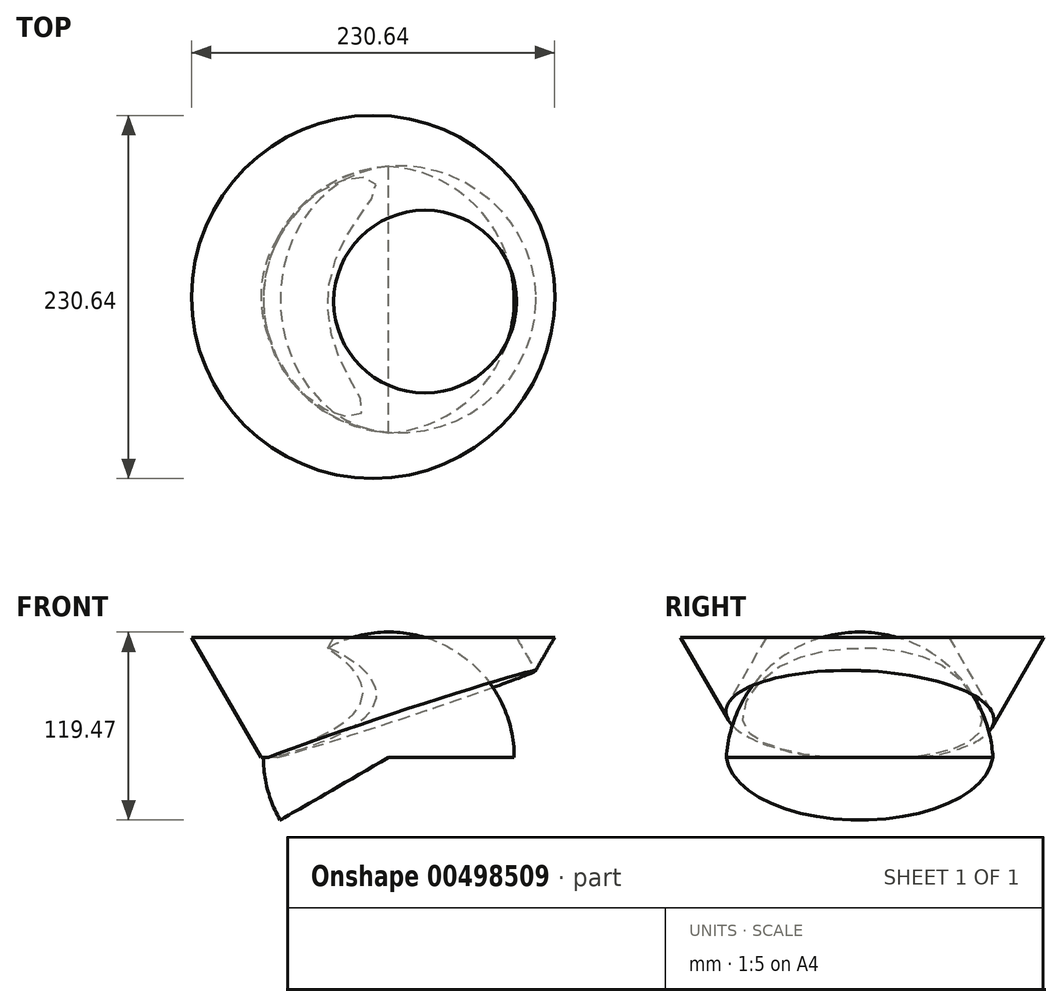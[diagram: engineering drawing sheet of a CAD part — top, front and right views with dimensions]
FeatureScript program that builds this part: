
annotation { "Feature Type Name" : "Feature", "Feature Type Description" : "" }
export const myFeature = defineFeature(function(context is Context, id is Id, definition is map)
    precondition{}
    {
        {
            var Q0;
            Q0=qCreatedBy(makeId("Top.planeOp"),FACE);
            var sketch = newSketch(context, id + "F0", { "sketchPlane" : qUnion([Q0])});
            skArc(sketch, "E0", {"start": v(5.72, 63.65) * mm, "mid": v(-4.67, 32.5) * mm, "end": v(0, 0) * mm});
            skArc(sketch, "E1", {"start": v(5.72, 63.65) * mm, "mid": v(-2.25, 32.28) * mm, "end": v(0, 0) * mm});
            skSolve(sketch);
        }
        {
            var Q0;
            Q0=makeQuery(id+"F0.imprint","IMPRINT",FACE,{"disambiguationData":[TD([[makeQuery(id+"F0.imprint","IMPRINT",EDGE,{"derivedFrom":sQuery(id+"F0.wireOp",EDGE,"E0")}),1.0]])]});
            extrude(context, id + "F1", {"entities" : qUnion([Q0]), "depth" : 76.2 * mm, "offsetDistance" : 25.4 * mm, "hasDraft" : true, "draftAngle" : 30 * degree});
        }
        {
            var Q0;
            Q0=qCreatedBy(makeId("Top.planeOp"),FACE);
            var sketch = newSketch(context, id + "F2", { "sketchPlane" : qUnion([Q0])});
            skLineSegment(sketch, "E2", {"start": v(76.3, -60.18) * mm, "end": v(76.3, 109.07) * mm});
            skArc(sketch, "E3", {"start": v(76.3, 109.07) * mm, "mid": v(-3.35, 24.44) * mm, "end": v(76.3, -60.18) * mm});
            skSolve(sketch);
        }
        {
            var Q0;
            Q0=makeQuery(id+"F2.imprint","IMPRINT",FACE,{"disambiguationData":[TD([[makeQuery(id+"F2.imprint","IMPRINT",EDGE,{"derivedFrom":sQuery(id+"F2.wireOp",EDGE,"E2")}),1.0]])]});
            var Q1;
            Q1=sQuery(id+"F2.wireOp",EDGE,"E2");
            revolve(context, id + "F3", {"operationType" : NewBodyOperationType.ADD, "entities" : qUnion([Q0]), "axis" : qUnion([Q1]), "revolveType" : RevolveType.TWO_DIRECTIONS, "angle" : 180 * degree, "angleBack" : 330 * degree});
        }
    });
